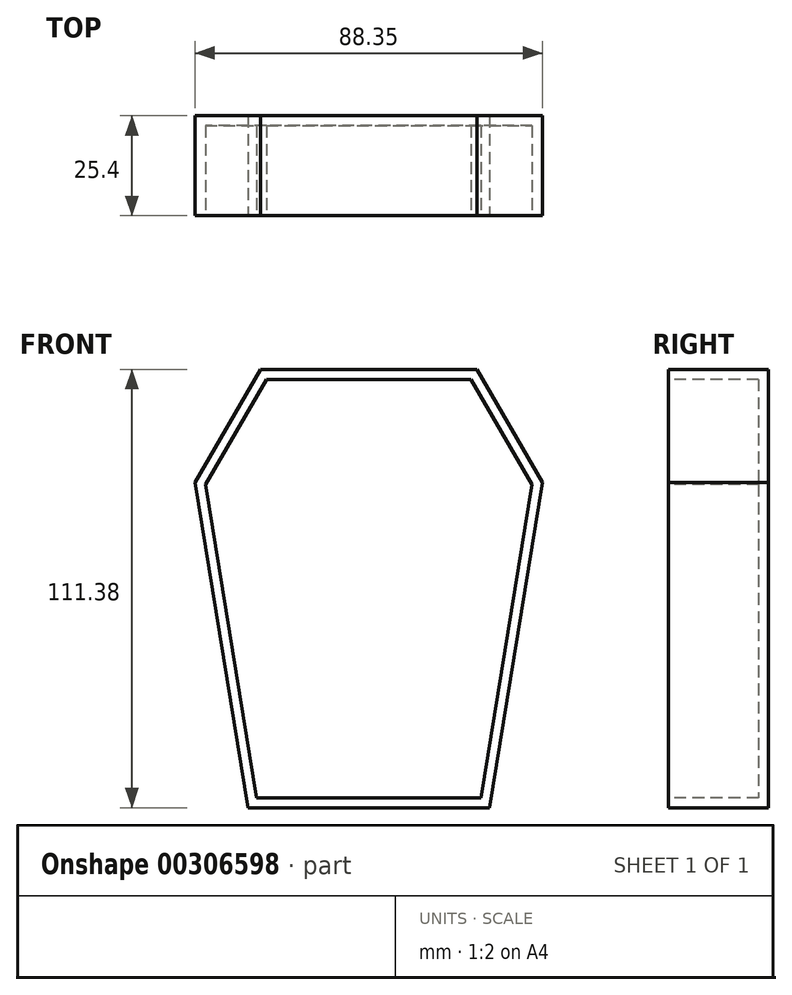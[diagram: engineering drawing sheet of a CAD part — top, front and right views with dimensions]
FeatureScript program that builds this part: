
annotation { "Feature Type Name" : "Feature", "Feature Type Description" : "" }
export const myFeature = defineFeature(function(context is Context, id is Id, definition is map)
    precondition{}
    {
        {
            var Q0;
            Q0=qCreatedBy(makeId("Front.planeOp"),FACE);
            var sketch = newSketch(context, id + "F0", { "sketchPlane" : qUnion([Q0])});
            skLineSegment(sketch, "E0", {"start": v(-27.34, 55.26) * mm, "end": v(27.63, 55.26) * mm});
            skLineSegment(sketch, "E1", {"start": v(27.63, 55.26) * mm, "end": v(44.32, 26.48) * mm});
            skLineSegment(sketch, "E2", {"start": v(-27.34, 55.26) * mm, "end": v(-44.03, 26.48) * mm});
            skLineSegment(sketch, "E3", {"start": v(44.32, 26.48) * mm, "end": v(30.8, -56.12) * mm});
            skLineSegment(sketch, "E4", {"start": v(-44.03, 26.48) * mm, "end": v(-30.5, -56.12) * mm});
            skLineSegment(sketch, "E5", {"start": v(30.8, -56.12) * mm, "end": v(-30.5, -56.12) * mm});
            skLineSegment(sketch, "E6", {"start": v(-30.5, -56.12) * mm, "end": v(-54.42, -60.04) * mm});
            skLineSegment(sketch, "E7", {"start": v(-54.42, -60.04) * mm, "end": v(-65.33, 22.74) * mm});
            skLineSegment(sketch, "E8", {"start": v(-65.33, 22.74) * mm, "end": v(-44.03, 26.48) * mm});
            skLineSegment(sketch, "E9", {"start": v(-65.33, 22.74) * mm, "end": v(-44.03, 56.4) * mm});
            skSolve(sketch);
        }
        {
            var Q0;
            Q0=makeQuery(id+"F0.imprint","IMPRINT",FACE,{"disambiguationData":[TD([[makeQuery(id+"F0.imprint","IMPRINT",EDGE,{"derivedFrom":sQuery(id+"F0.wireOp",EDGE,"E0")}),-1.0]])]});
            var sketch = newSketch(context, id + "F1", { "sketchPlane" : qUnion([Q0])});
            skSolve(sketch);
        }
        {
            var Q0;
            Q0=makeQuery(id+"F0.imprint","IMPRINT",FACE,{"disambiguationData":[TD([[makeQuery(id+"F0.imprint","IMPRINT",EDGE,{"derivedFrom":sQuery(id+"F0.wireOp",EDGE,"E0")}),-1.0]])]});
            extrude(context, id + "F2", {"entities" : qUnion([Q0]), "oppositeDirection" : true, "depth" : 25.4 * mm});
        }
        {
            var Q0;
            Q0=makeQuery(id+"F2.opExtrude","CAP_FACE",FACE,{"disambiguationData":[OSD([sQuery(id+"F0.wireOp",EDGE,"E0"),sQuery(id+"F0.wireOp",EDGE,"E1"),sQuery(id+"F0.wireOp",EDGE,"E2"),sQuery(id+"F0.wireOp",EDGE,"E3"),sQuery(id+"F0.wireOp",EDGE,"E4"),sQuery(id+"F0.wireOp",EDGE,"E5")])],"isStart":true});
            shell(context, id + "F3", {"entities" : qUnion([Q0]), "thickness" : 2.54 * mm});
        }
    });
